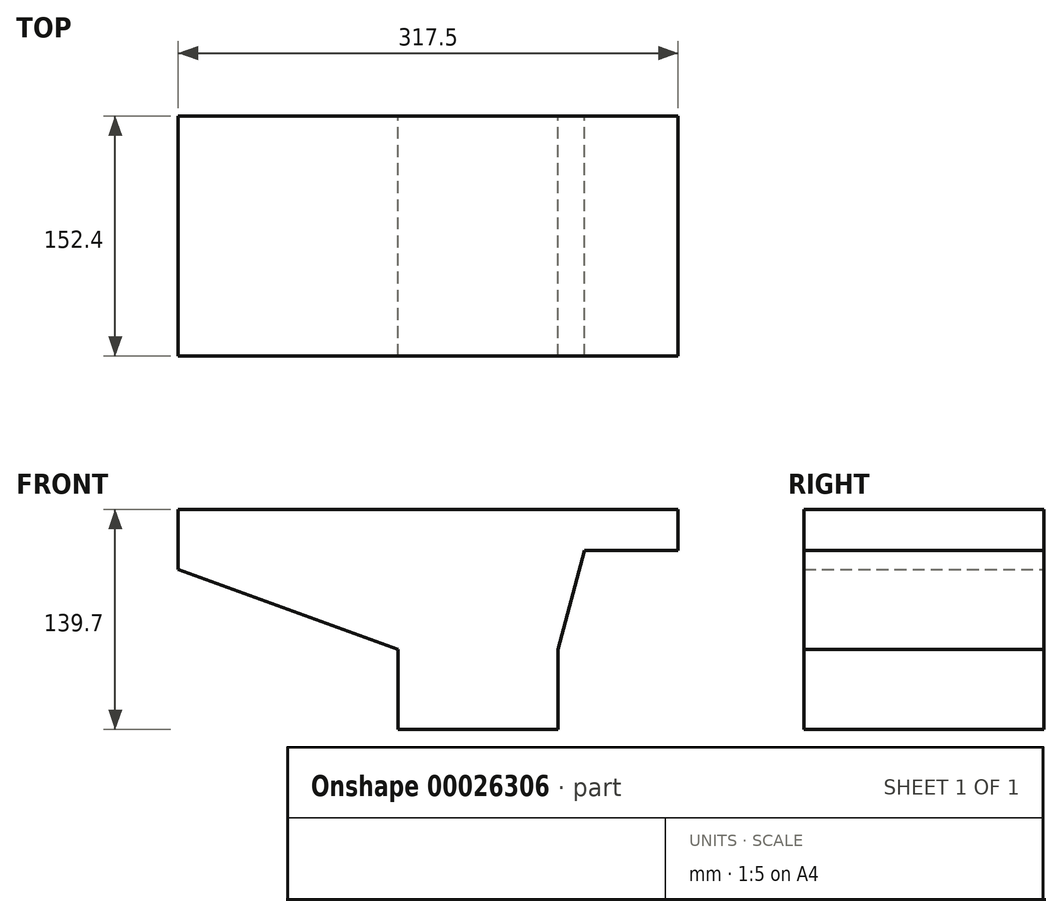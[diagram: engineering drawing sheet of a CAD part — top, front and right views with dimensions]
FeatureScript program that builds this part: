
annotation { "Feature Type Name" : "Feature", "Feature Type Description" : "" }
export const myFeature = defineFeature(function(context is Context, id is Id, definition is map)
    precondition{}
    {
        {
            var Q0;
            Q0=qCreatedBy(makeId("Front.planeOp"),FACE);
            var sketch = newSketch(context, id + "F0", { "sketchPlane" : qUnion([Q0])});
            skLineSegment(sketch, "E0", {"start": v(0, 0) * mm, "end": v(0, 50.8) * mm});
            skLineSegment(sketch, "E1", {"start": v(0, 50.8) * mm, "end": v(-139.57, 101.6) * mm});
            skLineSegment(sketch, "E2", {"start": v(-139.57, 101.6) * mm, "end": v(-139.57, 139.7) * mm});
            skLineSegment(sketch, "E3", {"start": v(-139.57, 139.7) * mm, "end": v(177.93, 139.7) * mm});
            skLineSegment(sketch, "E4", {"start": v(101.6, 50.8) * mm, "end": v(101.6, 0) * mm});
            skLineSegment(sketch, "E5", {"start": v(101.6, 0) * mm, "end": v(0, 0) * mm});
            skLineSegment(sketch, "E6", {"start": v(118.48, 113.8) * mm, "end": v(101.6, 50.8) * mm});
            skLineSegment(sketch, "E7", {"start": v(118.48, 113.8) * mm, "end": v(177.93, 113.8) * mm});
            skLineSegment(sketch, "E8", {"start": v(177.93, 113.8) * mm, "end": v(177.93, 139.7) * mm});
            skSolve(sketch);
        }
        {
            var Q0;
            Q0=makeQuery(id+"F0.imprint","IMPRINT",FACE,{"disambiguationData":[TD([[makeQuery(id+"F0.imprint","IMPRINT",EDGE,{"derivedFrom":sQuery(id+"F0.wireOp",EDGE,"E0")}),-1.0]])]});
            extrude(context, id + "F1", {"entities" : qUnion([Q0]), "endBound" : BoundingType.SYMMETRIC, "depth" : 152.4 * mm});
        }
    });
